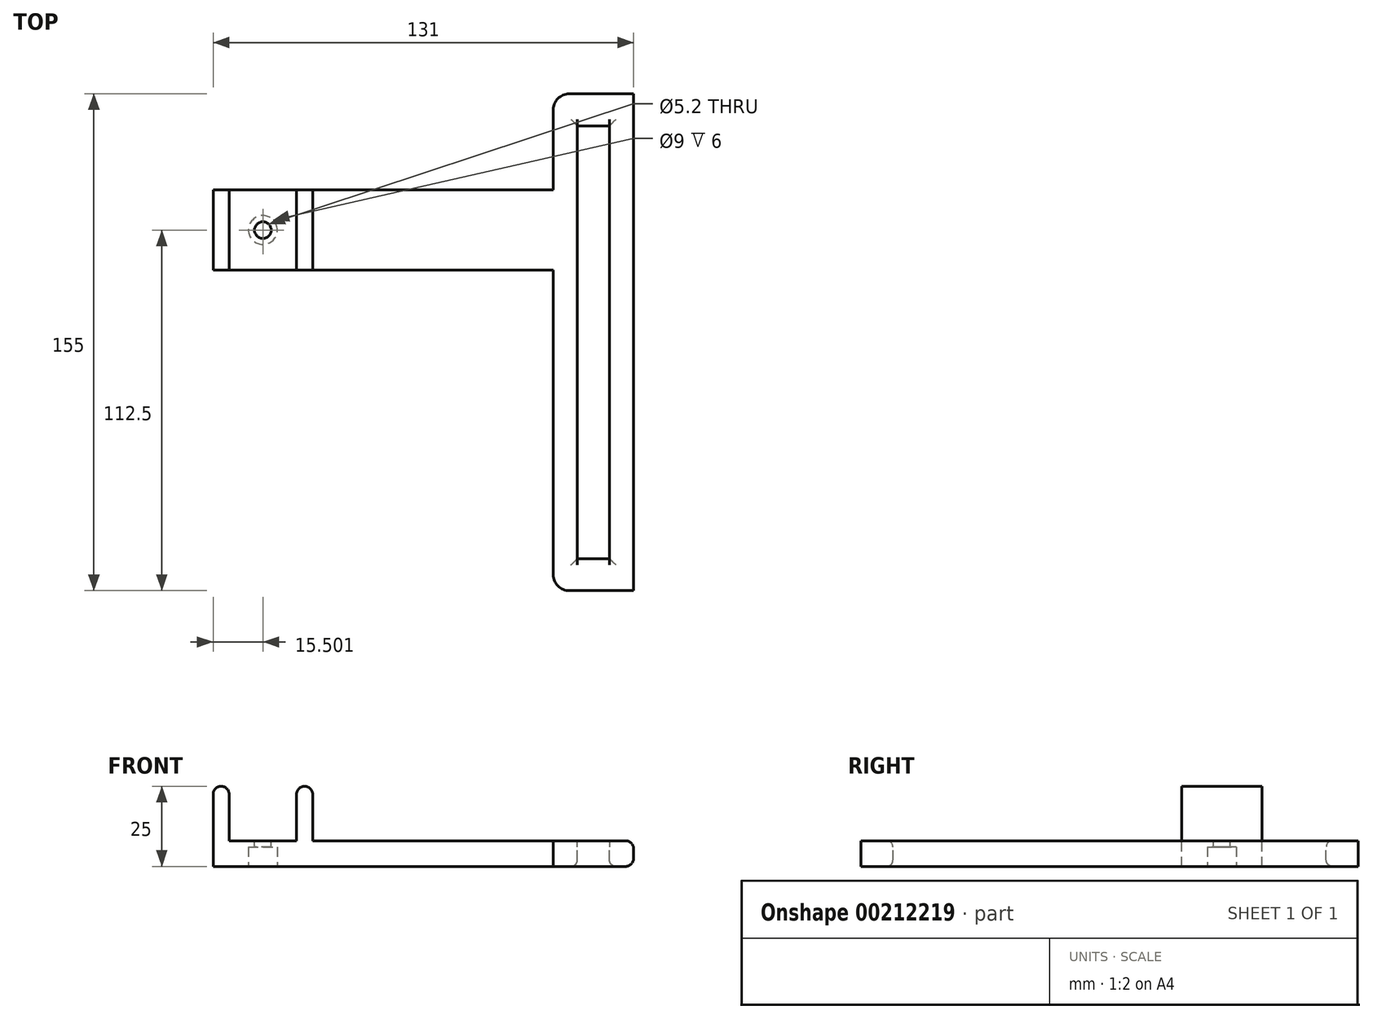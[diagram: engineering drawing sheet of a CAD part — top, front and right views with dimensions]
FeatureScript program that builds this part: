
annotation { "Feature Type Name" : "Feature", "Feature Type Description" : "" }
export const myFeature = defineFeature(function(context is Context, id is Id, definition is map)
    precondition{}
    {
        {
            var Q0;
            Q0=qCreatedBy(makeId("Front.planeOp"),FACE);
            var sketch = newSketch(context, id + "F0", { "sketchPlane" : qUnion([Q0])});
            skLineSegment(sketch, "E0.bottom", {"start": v(-18.72, 0) * mm, "end": v(12.28, 0) * mm});
            skLineSegment(sketch, "E0.top", {"start": v(-18.72, 8) * mm, "end": v(12.28, 8) * mm});
            skLineSegment(sketch, "E0.left", {"start": v(-18.72, 0) * mm, "end": v(-18.72, 8) * mm});
            skLineSegment(sketch, "E0.right", {"start": v(12.28, 0) * mm, "end": v(12.28, 8) * mm});
            skLineSegment(sketch, "E1.bottom", {"start": v(-18.72, 0) * mm, "end": v(-13.72, 0) * mm});
            skLineSegment(sketch, "E1.top", {"start": v(-18.72, 25) * mm, "end": v(-13.72, 25) * mm});
            skLineSegment(sketch, "E1.left", {"start": v(-18.72, 0) * mm, "end": v(-18.72, 25) * mm});
            skLineSegment(sketch, "E1.right", {"start": v(-13.72, 0) * mm, "end": v(-13.72, 25) * mm});
            skLineSegment(sketch, "E2.bottom", {"start": v(12.28, 0) * mm, "end": v(7.28, 0) * mm});
            skLineSegment(sketch, "E2.top", {"start": v(12.28, 25) * mm, "end": v(7.28, 25) * mm});
            skLineSegment(sketch, "E2.left", {"start": v(12.28, 0) * mm, "end": v(12.28, 25) * mm});
            skLineSegment(sketch, "E2.right", {"start": v(7.28, 0) * mm, "end": v(7.28, 25) * mm});
            skLineSegment(sketch, "E3.bottom", {"start": v(12.28, 8) * mm, "end": v(112.28, 8) * mm});
            skLineSegment(sketch, "E3.top", {"start": v(12.28, 0) * mm, "end": v(112.28, 0) * mm});
            skLineSegment(sketch, "E3.left", {"start": v(12.28, 8) * mm, "end": v(12.28, 0) * mm});
            skLineSegment(sketch, "E3.right", {"start": v(112.28, 8) * mm, "end": v(112.28, 0) * mm});
            skSolve(sketch);
        }
        {
            var Q0;
            {var subQ5=sQuery(id+"F0.wireOp",EDGE,"E1.top");Q0=makeQuery(id+"F0.imprint","IMPRINT",FACE,{"disambiguationData":[TD([[makeQuery(id+"F0.imprint","IMPRINT",EDGE,{"derivedFrom":subQ5}),-1.0]])]});}
            var Q1;
            {var subQ5=sQuery(id+"F0.wireOp",EDGE,"E1.bottom");Q1=makeQuery(id+"F0.imprint","IMPRINT",FACE,{"disambiguationData":[TD([[makeQuery(id+"F0.imprint","IMPRINT",EDGE,{"derivedFrom":subQ5}),1.0]])]});}
            var Q2;
            {var subQ0=sQuery(id+"F0.wireOp",EDGE,"E0.bottom");Q2=makeQuery(id+"F0.imprint","IMPRINT",FACE,{"disambiguationData":[TD([[makeQuery(id+"F0.imprint","IMPRINT",EDGE,{"derivedFrom":subQ0}),1.0]])]});}
            var Q3;
            {var subQ4=sQuery(id+"F0.wireOp",EDGE,"E2.bottom");Q3=makeQuery(id+"F0.imprint","IMPRINT",FACE,{"disambiguationData":[TD([[makeQuery(id+"F0.imprint","IMPRINT",EDGE,{"derivedFrom":subQ4}),-1.0]])]});}
            var Q4;
            {var subQ4=sQuery(id+"F0.wireOp",EDGE,"E2.top");Q4=makeQuery(id+"F0.imprint","IMPRINT",FACE,{"disambiguationData":[TD([[makeQuery(id+"F0.imprint","IMPRINT",EDGE,{"derivedFrom":subQ4}),1.0]])]});}
            var Q5;
            Q5=makeQuery(id+"F0.imprint","IMPRINT",FACE,{"disambiguationData":[TD([[makeQuery(id+"F0.imprint","IMPRINT",EDGE,{"derivedFrom":sQuery(id+"F0.wireOp",EDGE,"E3.bottom")}),-1.0]])]});
            extrude(context, id + "F1", {"entities" : qUnion([Q0, Q1, Q2, Q3, Q4, Q5]), "depth" : 25 * mm});
        }
        {
            var Q0;
            Q0=makeQuery(id+"F1.opExtrude","SWEPT_FACE",FACE,{"disambiguationData":[OSD([sQuery(id+"F0.wireOp",EDGE,"E3.bottom")])]});
            var sketch = newSketch(context, id + "F2", { "sketchPlane" : qUnion([Q0])});
            skPoint(sketch, "E4.firstSnap0", {"position": v(112.28, -12.5) * mm});
            skLineSegment(sketch, "E4.bottom", {"start": v(112.28, -125) * mm, "end": v(87.28, -125) * mm});
            skLineSegment(sketch, "E4.top", {"start": v(112.28, 30) * mm, "end": v(87.28, 30) * mm});
            skLineSegment(sketch, "E4.left", {"start": v(112.28, -125) * mm, "end": v(112.28, 30) * mm});
            skLineSegment(sketch, "E4.right", {"start": v(87.28, -125) * mm, "end": v(87.28, 30) * mm});
            skLineSegment(sketch, "E5.bottom", {"start": v(94.78, 20) * mm, "end": v(104.78, 20) * mm});
            skLineSegment(sketch, "E5.top", {"start": v(94.78, -115) * mm, "end": v(104.78, -115) * mm});
            skLineSegment(sketch, "E5.left", {"start": v(94.78, 20) * mm, "end": v(94.78, -115) * mm});
            skLineSegment(sketch, "E5.right", {"start": v(104.78, 20) * mm, "end": v(104.78, -115) * mm});
            skSolve(sketch);
        }
        {
            var Q0;
            {var subQ0=sQuery(id+"F2.wireOp",EDGE,"E4.bottom");Q0=makeQuery(id+"F2.imprint","IMPRINT",FACE,{"disambiguationData":[TD([[makeQuery(id+"F2.imprint","IMPRINT",EDGE,{"derivedFrom":subQ0}),-1.0]])]});}
            var Q1;
            {var subQ0=sQuery(id+"F2.wireOp",EDGE,"E4.top");Q1=makeQuery(id+"F2.imprint","IMPRINT",FACE,{"disambiguationData":[TD([[makeQuery(id+"F2.imprint","IMPRINT",EDGE,{"derivedFrom":subQ0}),1.0]])]});}
            extrude(context, id + "F3", {"entities" : qUnion([Q0, Q1]), "operationType" : NewBodyOperationType.ADD, "oppositeDirection" : true, "depth" : 8 * mm});
        }
        {
            var Q0;
            {var subQ0=sQuery(id+"F2.wireOp",EDGE,"E4.left");var subQ1=sQuery(id+"F0.wireOp",EDGE,"E3.bottom");Q0=makeQuery(id+"F3.boolean.opBoolean","MERGE",EDGE,{"derivedFrom":[makeQuery(id+"F1.opExtrude","SWEPT_EDGE",EDGE,{"disambiguationData":[OSD([sQuery(id+"F0.wireOp",EDGE,"E3.top"),sQuery(id+"F0.wireOp",EDGE,"E3.right")])]}),makeQuery(id+"F3.opExtrude","CAP_EDGE",EDGE,{"disambiguationData":[OSD([subQ0]),TDD([makeQuery(id+"F2.imprint","IMPRINT",EDGE,{"disambiguationData":[TD([[makeQuery(id+"F2.imprint","INTERSECT",VERTEX,{"derivedFrom":[makeQuery(id+"F1.opExtrude","CAP_EDGE",EDGE,{"disambiguationData":[OSD([subQ1])],"isStart":false}),subQ0]}),1.0]])],"derivedFrom":subQ0})])],"isStart":false}),makeQuery(id+"F3.opExtrude","CAP_EDGE",EDGE,{"disambiguationData":[OSD([subQ0]),TDD([makeQuery(id+"F2.imprint","IMPRINT",EDGE,{"disambiguationData":[TD([[makeQuery(id+"F2.imprint","INTERSECT",VERTEX,{"derivedFrom":[makeQuery(id+"F1.opExtrude","CAP_EDGE",EDGE,{"disambiguationData":[OSD([subQ1])],"isStart":true}),subQ0]}),-1.0]])],"derivedFrom":subQ0})])],"isStart":false})]});}
            var Q1;
            {var subQ0=sQuery(id+"F2.wireOp",EDGE,"E4.left");var subQ1=sQuery(id+"F0.wireOp",EDGE,"E3.bottom");Q1=makeQuery(id+"F3.boolean.opBoolean","MERGE",EDGE,{"derivedFrom":[makeQuery(id+"F1.opExtrude","SWEPT_EDGE",EDGE,{"disambiguationData":[OSD([subQ1,sQuery(id+"F0.wireOp",EDGE,"E3.right")])]}),makeQuery(id+"F3.opExtrude","CAP_EDGE",EDGE,{"disambiguationData":[OSD([subQ0]),TDD([makeQuery(id+"F2.imprint","IMPRINT",EDGE,{"disambiguationData":[TD([[makeQuery(id+"F2.imprint","INTERSECT",VERTEX,{"derivedFrom":[makeQuery(id+"F1.opExtrude","CAP_EDGE",EDGE,{"disambiguationData":[OSD([subQ1])],"isStart":false}),subQ0]}),1.0]])],"derivedFrom":subQ0})])],"isStart":true}),makeQuery(id+"F3.opExtrude","CAP_EDGE",EDGE,{"disambiguationData":[OSD([subQ0]),TDD([makeQuery(id+"F2.imprint","IMPRINT",EDGE,{"disambiguationData":[TD([[makeQuery(id+"F2.imprint","INTERSECT",VERTEX,{"derivedFrom":[makeQuery(id+"F1.opExtrude","CAP_EDGE",EDGE,{"disambiguationData":[OSD([subQ1])],"isStart":true}),subQ0]}),-1.0]])],"derivedFrom":subQ0})])],"isStart":true})]});}
            fillet(context, id + "F4", {"entities" : qUnion([Q0, Q1]), "radius" : 2.5 * mm, "tangentPropagation" : true, "allowEdgeOverflow" : false});
        }
        {
            var Q0;
            Q0=makeQuery(id+"F1.opExtrude","SWEPT_EDGE",EDGE,{"disambiguationData":[OSD([sQuery(id+"F0.wireOp",EDGE,"E2.top"),sQuery(id+"F0.wireOp",EDGE,"E2.left")])]});
            var Q1;
            Q1=makeQuery(id+"F1.opExtrude","SWEPT_EDGE",EDGE,{"disambiguationData":[OSD([sQuery(id+"F0.wireOp",EDGE,"E2.top"),sQuery(id+"F0.wireOp",EDGE,"E2.right")])]});
            var Q2;
            Q2=makeQuery(id+"F1.opExtrude","SWEPT_EDGE",EDGE,{"disambiguationData":[OSD([sQuery(id+"F0.wireOp",EDGE,"E1.top"),sQuery(id+"F0.wireOp",EDGE,"E1.left")])]});
            var Q3;
            Q3=makeQuery(id+"F1.opExtrude","SWEPT_EDGE",EDGE,{"disambiguationData":[OSD([sQuery(id+"F0.wireOp",EDGE,"E1.top"),sQuery(id+"F0.wireOp",EDGE,"E1.right")])]});
            fillet(context, id + "F5", {"entities" : qUnion([Q0, Q1, Q2, Q3]), "radius" : 2.5 * mm, "tangentPropagation" : true, "allowEdgeOverflow" : false});
        }
        {
            var Q0;
            Q0=makeQuery(id+"F1.opExtrude","SWEPT_FACE",FACE,{"disambiguationData":[OSD([sQuery(id+"F0.wireOp",EDGE,"E0.top")])]});
            var sketch = newSketch(context, id + "F6", { "sketchPlane" : qUnion([Q0])});
            skCircle(sketch, "E6", {"center": v(-3.22, -12.5) * mm, "radius": 2.6 * mm});
            skPoint(sketch, "E6.centerSnap0", {"position": v(-13.72, -12.5) * mm});
            skPoint(sketch, "E6.centerSnap1", {"position": v(-3.22, -25) * mm});
            skSolve(sketch);
        }
        {
            var Q0;
            Q0=makeQuery(id+"F6.imprint","IMPRINT",FACE,{"disambiguationData":[TD([[makeQuery(id+"F6.imprint","IMPRINT",EDGE,{"derivedFrom":sQuery(id+"F6.wireOp",EDGE,"E6")}),1.0]])]});
            extrude(context, id + "F7", {"entities" : qUnion([Q0]), "operationType" : NewBodyOperationType.REMOVE, "oppositeDirection" : true, "depth" : 25 * mm});
        }
        {
            var Q0;
            Q0=makeQuery(id+"F3.opExtrude","SWEPT_EDGE",EDGE,{"disambiguationData":[OSD([sQuery(id+"F2.wireOp",EDGE,"E4.top"),sQuery(id+"F2.wireOp",EDGE,"E4.right")])]});
            var Q1;
            Q1=makeQuery(id+"F3.opExtrude","SWEPT_EDGE",EDGE,{"disambiguationData":[OSD([sQuery(id+"F2.wireOp",EDGE,"E4.bottom"),sQuery(id+"F2.wireOp",EDGE,"E4.right")])]});
            fillet(context, id + "F8", {"entities" : qUnion([Q0, Q1]), "radius" : 5 * mm, "tangentPropagation" : true, "allowEdgeOverflow" : false});
        }
        {
            var Q0;
            {var subQ0=sQuery(id+"F2.wireOp",EDGE,"E4.right");var subQ1=sQuery(id+"F2.wireOp",EDGE,"E4.left");var subQ2=sQuery(id+"F0.wireOp",EDGE,"E3.bottom");Q0=makeQuery(id+"F3.boolean.opBoolean","MERGE",FACE,{"derivedFrom":[makeQuery(id+"F1.opExtrude","SWEPT_FACE",FACE,{"disambiguationData":[OSD([sQuery(id+"F0.wireOp",EDGE,"E0.bottom"),sQuery(id+"F0.wireOp",EDGE,"E1.bottom"),sQuery(id+"F0.wireOp",EDGE,"E2.bottom"),sQuery(id+"F0.wireOp",EDGE,"E3.top")])]}),makeQuery(id+"F3.opExtrude","CAP_FACE",FACE,{"disambiguationData":[OSD([subQ2,sQuery(id+"F2.wireOp",EDGE,"E4.bottom"),subQ1,subQ0])],"isStart":false}),makeQuery(id+"F3.opExtrude","CAP_FACE",FACE,{"disambiguationData":[OSD([subQ2,sQuery(id+"F2.wireOp",EDGE,"E4.top"),subQ1,subQ0])],"isStart":false})]});}
            var sketch = newSketch(context, id + "F9", { "sketchPlane" : qUnion([Q0])});
            skCircle(sketch, "E7", {"center": v(-3.22, 12.5) * mm, "radius": 4.5 * mm});
            skSolve(sketch);
        }
        {
            var Q0;
            Q0=makeQuery(id+"F9.imprint","IMPRINT",FACE,{"disambiguationData":[TD([[makeQuery(id+"F9.imprint","IMPRINT",EDGE,{"derivedFrom":sQuery(id+"F9.wireOp",EDGE,"E7")}),1.0]])]});
            extrude(context, id + "F10", {"entities" : qUnion([Q0]), "operationType" : NewBodyOperationType.REMOVE, "oppositeDirection" : true, "depth" : 6 * mm});
        }
        {
            var Q0;
            {var subQ0=sQuery(id+"F2.wireOp",EDGE,"E5.left");var subQ1=sQuery(id+"F0.wireOp",EDGE,"E3.bottom");var subQ2=makeQuery(id+"F1.opExtrude","CAP_EDGE",EDGE,{"disambiguationData":[OSD([subQ1])],"isStart":true});var subQ3=makeQuery(id+"F2.imprint","INTERSECT",VERTEX,{"derivedFrom":[subQ2,subQ0]});Q0=makeQuery(id+"F2.imprint","IMPRINT",FACE,{"disambiguationData":[TD([[makeQuery(id+"F2.imprint","IMPRINT",EDGE,{"disambiguationData":[TD([[subQ3,-1.0]])],"derivedFrom":subQ0}),1.0]])]});}
            extrude(context, id + "F11", {"entities" : qUnion([Q0]), "operationType" : NewBodyOperationType.REMOVE, "oppositeDirection" : true, "depth" : 25 * mm});
        }
        {
            var Q0;
            {var subQ0=sQuery(id+"F2.wireOp",EDGE,"E5.left");Q0=makeQuery(id+"F11.boolean.opBoolean","MERGE",EDGE,{"derivedFrom":[makeQuery(id+"F3.opExtrude","CAP_EDGE",EDGE,{"disambiguationData":[OSD([subQ0]),TDD([makeQuery(id+"F2.imprint","IMPRINT",EDGE,{"disambiguationData":[TD([[makeQuery(id+"F2.imprint","INTERSECT",VERTEX,{"derivedFrom":[sQuery(id+"F2.wireOp",EDGE,"E5.bottom"),subQ0]}),-1.0]])],"derivedFrom":subQ0})])],"isStart":true}),makeQuery(id+"F3.opExtrude","CAP_EDGE",EDGE,{"disambiguationData":[OSD([subQ0]),TDD([makeQuery(id+"F2.imprint","IMPRINT",EDGE,{"disambiguationData":[TD([[makeQuery(id+"F2.imprint","INTERSECT",VERTEX,{"derivedFrom":[sQuery(id+"F2.wireOp",EDGE,"E5.top"),subQ0]}),1.0]])],"derivedFrom":subQ0})])],"isStart":true}),makeQuery(id+"F11.opExtrude","CAP_EDGE",EDGE,{"disambiguationData":[OSD([subQ0])],"isStart":true})]});}
            var Q1;
            Q1=makeQuery(id+"F3.opExtrude","CAP_EDGE",EDGE,{"disambiguationData":[OSD([sQuery(id+"F2.wireOp",EDGE,"E5.bottom")])],"isStart":true});
            var Q2;
            {var subQ0=sQuery(id+"F2.wireOp",EDGE,"E5.right");Q2=makeQuery(id+"F11.boolean.opBoolean","MERGE",EDGE,{"derivedFrom":[makeQuery(id+"F3.opExtrude","CAP_EDGE",EDGE,{"disambiguationData":[OSD([subQ0]),TDD([makeQuery(id+"F2.imprint","IMPRINT",EDGE,{"disambiguationData":[TD([[makeQuery(id+"F2.imprint","INTERSECT",VERTEX,{"derivedFrom":[sQuery(id+"F2.wireOp",EDGE,"E5.bottom"),subQ0]}),-1.0]])],"derivedFrom":subQ0})])],"isStart":true}),makeQuery(id+"F3.opExtrude","CAP_EDGE",EDGE,{"disambiguationData":[OSD([subQ0]),TDD([makeQuery(id+"F2.imprint","IMPRINT",EDGE,{"disambiguationData":[TD([[makeQuery(id+"F2.imprint","INTERSECT",VERTEX,{"derivedFrom":[sQuery(id+"F2.wireOp",EDGE,"E5.top"),subQ0]}),1.0]])],"derivedFrom":subQ0})])],"isStart":true}),makeQuery(id+"F11.opExtrude","CAP_EDGE",EDGE,{"disambiguationData":[OSD([subQ0])],"isStart":true})]});}
            var Q3;
            Q3=makeQuery(id+"F3.opExtrude","CAP_EDGE",EDGE,{"disambiguationData":[OSD([sQuery(id+"F2.wireOp",EDGE,"E5.top")])],"isStart":true});
            var Q4;
            Q4=makeQuery(id+"F3.opExtrude","CAP_EDGE",EDGE,{"disambiguationData":[OSD([sQuery(id+"F2.wireOp",EDGE,"E5.bottom")])],"isStart":false});
            var Q5;
            {var subQ0=sQuery(id+"F2.wireOp",EDGE,"E5.left");var subQ1=sQuery(id+"F2.wireOp",EDGE,"E5.right");var subQ2=sQuery(id+"F2.wireOp",EDGE,"E4.right");var subQ3=sQuery(id+"F2.wireOp",EDGE,"E4.left");var subQ4=sQuery(id+"F0.wireOp",EDGE,"E3.bottom");Q5=makeQuery(id+"F11.boolean.opBoolean","INTERSECT",EDGE,{"derivedFrom":[makeQuery(id+"F3.boolean.opBoolean","MERGE",FACE,{"derivedFrom":[makeQuery(id+"F1.opExtrude","SWEPT_FACE",FACE,{"disambiguationData":[OSD([sQuery(id+"F0.wireOp",EDGE,"E0.bottom"),sQuery(id+"F0.wireOp",EDGE,"E1.bottom"),sQuery(id+"F0.wireOp",EDGE,"E2.bottom"),sQuery(id+"F0.wireOp",EDGE,"E3.top")])]}),makeQuery(id+"F3.opExtrude","CAP_FACE",FACE,{"disambiguationData":[OSD([subQ4,sQuery(id+"F2.wireOp",EDGE,"E4.bottom"),subQ3,subQ2,sQuery(id+"F2.wireOp",EDGE,"E5.top"),subQ0,subQ1])],"isStart":false}),makeQuery(id+"F3.opExtrude","CAP_FACE",FACE,{"disambiguationData":[OSD([subQ4,sQuery(id+"F2.wireOp",EDGE,"E4.top"),subQ3,subQ2,sQuery(id+"F2.wireOp",EDGE,"E5.bottom"),subQ0,subQ1])],"isStart":false})]}),makeQuery(id+"F11.opExtrude","SWEPT_FACE",FACE,{"disambiguationData":[OSD([subQ0])]})]});}
            var Q6;
            {var subQ0=sQuery(id+"F2.wireOp",EDGE,"E5.right");var subQ1=sQuery(id+"F2.wireOp",EDGE,"E5.left");var subQ2=sQuery(id+"F2.wireOp",EDGE,"E4.right");var subQ3=sQuery(id+"F2.wireOp",EDGE,"E4.left");var subQ4=sQuery(id+"F0.wireOp",EDGE,"E3.bottom");Q6=makeQuery(id+"F11.boolean.opBoolean","INTERSECT",EDGE,{"derivedFrom":[makeQuery(id+"F3.boolean.opBoolean","MERGE",FACE,{"derivedFrom":[makeQuery(id+"F1.opExtrude","SWEPT_FACE",FACE,{"disambiguationData":[OSD([sQuery(id+"F0.wireOp",EDGE,"E0.bottom"),sQuery(id+"F0.wireOp",EDGE,"E1.bottom"),sQuery(id+"F0.wireOp",EDGE,"E2.bottom"),sQuery(id+"F0.wireOp",EDGE,"E3.top")])]}),makeQuery(id+"F3.opExtrude","CAP_FACE",FACE,{"disambiguationData":[OSD([subQ4,sQuery(id+"F2.wireOp",EDGE,"E4.bottom"),subQ3,subQ2,sQuery(id+"F2.wireOp",EDGE,"E5.top"),subQ1,subQ0])],"isStart":false}),makeQuery(id+"F3.opExtrude","CAP_FACE",FACE,{"disambiguationData":[OSD([subQ4,sQuery(id+"F2.wireOp",EDGE,"E4.top"),subQ3,subQ2,sQuery(id+"F2.wireOp",EDGE,"E5.bottom"),subQ1,subQ0])],"isStart":false})]}),makeQuery(id+"F11.opExtrude","SWEPT_FACE",FACE,{"disambiguationData":[OSD([subQ0])]})]});}
            var Q7;
            Q7=makeQuery(id+"F3.opExtrude","CAP_EDGE",EDGE,{"disambiguationData":[OSD([sQuery(id+"F2.wireOp",EDGE,"E5.top")])],"isStart":false});
            fillet(context, id + "F12", {"entities" : qUnion([Q0, Q1, Q2, Q3, Q4, Q5, Q6, Q7]), "radius" : 2 * mm, "tangentPropagation" : true, "allowEdgeOverflow" : false});
        }
    });
